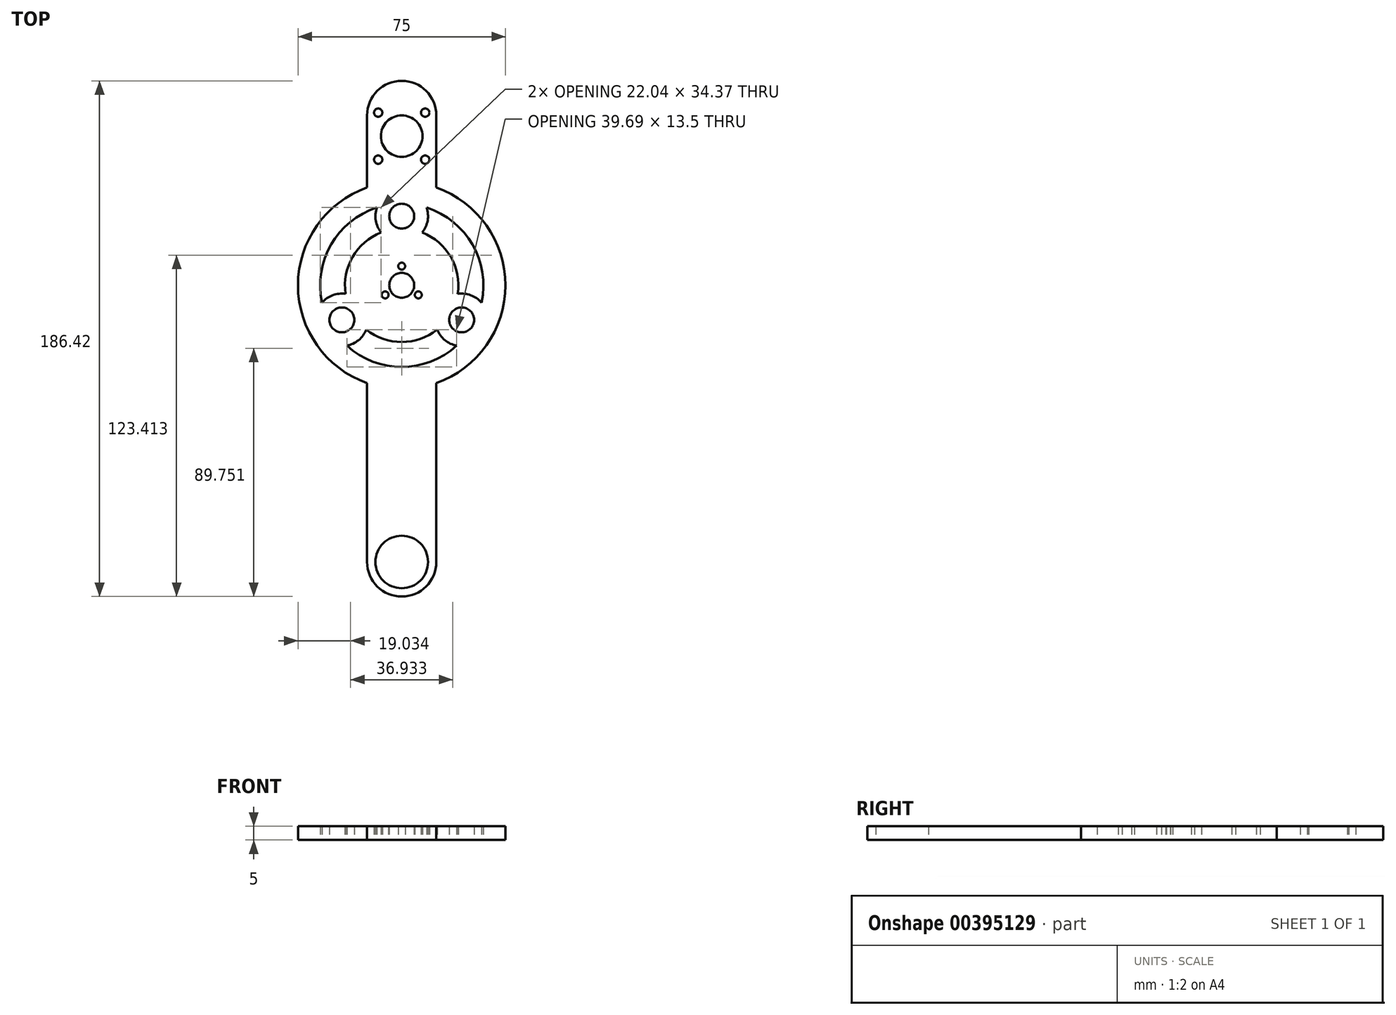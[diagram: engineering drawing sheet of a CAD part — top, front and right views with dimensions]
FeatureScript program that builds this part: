
annotation { "Feature Type Name" : "Feature", "Feature Type Description" : "" }
export const myFeature = defineFeature(function(context is Context, id is Id, definition is map)
    precondition{}
    {
        {
            var Q0;
            Q0=qCreatedBy(makeId("Top.planeOp"),FACE);
            var sketch = newSketch(context, id + "F0", { "sketchPlane" : qUnion([Q0])});
            skCircle(sketch, "E0", {"center": v(0, 0) * mm, "radius": 37.5 * mm});
            skLineSegment(sketch, "E1", {"start": v(-12.5, 35.36) * mm, "end": v(-12.5, 61.42) * mm});
            skArc(sketch, "E2", {"start": v(12.5, 61.42) * mm, "mid": v(0, 73.92) * mm, "end": v(-12.5, 61.42) * mm});
            skLineSegment(sketch, "E3", {"start": v(12.5, 61.42) * mm, "end": v(12.5, 35.36) * mm});
            skLineSegment(sketch, "E4", {"start": v(-12.5, -35.36) * mm, "end": v(-12.5, -100) * mm});
            skArc(sketch, "E5", {"start": v(-12.5, -100) * mm, "mid": v(0, -112.5) * mm, "end": v(12.5, -100) * mm});
            skLineSegment(sketch, "E6", {"start": v(12.5, -100) * mm, "end": v(12.5, -35.36) * mm});
            skCircle(sketch, "E7", {"center": v(-8.5, 45.42) * mm, "radius": 1.5 * mm});
            skCircle(sketch, "E8", {"center": v(8.5, 45.42) * mm, "radius": 1.5 * mm});
            skCircle(sketch, "E9", {"center": v(0, 53.92) * mm, "radius": 7.5 * mm});
            skCircle(sketch, "E10", {"center": v(8.5, 62.42) * mm, "radius": 1.5 * mm});
            skLineSegment(sketch, "E11", {"start": v(8.5, 45.42) * mm, "end": v(0, 53.92) * mm, "construction": true});
            skCircle(sketch, "E12", {"center": v(-8.5, 62.42) * mm, "radius": 1.5 * mm});
            skLineSegment(sketch, "E13", {"start": v(-8.5, 45.42) * mm, "end": v(0, 53.92) * mm, "construction": true});
            skLineSegment(sketch, "E14", {"start": v(-8.5, 62.42) * mm, "end": v(0, 53.92) * mm, "construction": true});
            skLineSegment(sketch, "E15", {"start": v(-12.5, 35.36) * mm, "end": v(12.5, 35.36) * mm, "construction": true});
            skLineSegment(sketch, "E16", {"start": v(12.5, -35.36) * mm, "end": v(-12.5, -35.36) * mm, "construction": true});
            skLineSegment(sketch, "E17", {"start": v(0, 0) * mm, "end": v(0, -18.97) * mm, "construction": true});
            skCircle(sketch, "E18", {"center": v(0, 0) * mm, "radius": 4.5 * mm});
            skLineSegment(sketch, "E19", {"start": v(8.5, 62.42) * mm, "end": v(0, 53.92) * mm, "construction": true});
            skCircle(sketch, "E20", {"center": v(0, -100) * mm, "radius": 9.5 * mm});
            skCircle(sketch, "E21", {"center": v(0, 6.93) * mm, "radius": 1.25 * mm});
            skCircle(sketch, "E22", {"center": v(6, -3.46) * mm, "radius": 1.25 * mm});
            skCircle(sketch, "E23", {"center": v(-6, -3.46) * mm, "radius": 1.25 * mm});
            skCircle(sketch, "E24", {"center": v(0, 0) * mm, "radius": 10 * mm});
            skLineSegment(sketch, "E25", {"start": v(-6, -3.46) * mm, "end": v(0, 6.93) * mm, "construction": true});
            skLineSegment(sketch, "E26", {"start": v(6, -3.46) * mm, "end": v(0, 6.93) * mm, "construction": true});
            skLineSegment(sketch, "E27", {"start": v(-6, -3.46) * mm, "end": v(6, -3.46) * mm, "construction": true});
            skLineSegment(sketch, "E28", {"start": v(-6, -3.46) * mm, "end": v(0, 0) * mm, "construction": true});
            skLineSegment(sketch, "E29", {"start": v(0, 6.93) * mm, "end": v(0, 0) * mm, "construction": true});
            skLineSegment(sketch, "E30", {"start": v(0, 0) * mm, "end": v(6, -3.46) * mm, "construction": true});
            skCircle(sketch, "E31", {"center": v(0, 25) * mm, "radius": 4.5 * mm});
            skCircle(sketch, "E32", {"center": v(21.65, -12.5) * mm, "radius": 4.5 * mm});
            skCircle(sketch, "E33", {"center": v(-21.65, -12.5) * mm, "radius": 4.5 * mm});
            skLineSegment(sketch, "E34", {"start": v(0, 25) * mm, "end": v(0, 6.93) * mm, "construction": true});
            skLineSegment(sketch, "E35", {"start": v(-21.65, -12.5) * mm, "end": v(-6, -3.46) * mm, "construction": true});
            skLineSegment(sketch, "E36", {"start": v(21.65, -12.5) * mm, "end": v(6, -3.46) * mm, "construction": true});
            skCircle(sketch, "E37", {"center": v(0, 25) * mm, "radius": 9.5 * mm});
            skCircle(sketch, "E38", {"center": v(-21.65, -12.5) * mm, "radius": 9.5 * mm});
            skCircle(sketch, "E39", {"center": v(21.65, -12.5) * mm, "radius": 9.5 * mm});
            skCircle(sketch, "E40", {"center": v(0, 0) * mm, "radius": 20.5 * mm});
            skCircle(sketch, "E41", {"center": v(0, 0) * mm, "radius": 29.5 * mm});
            skSolve(sketch);
        }
        {
            var Q0;
            Q0=qSketchRegion(id+"F0",true);
            var Q1;
            {var subQ0=sQuery(id+"F0.wireOp",EDGE,"55e76af4-ff7d-4902-8194-23b5d1213256");var subQ2=sQuery(id+"F0.wireOp",EDGE,"25387a36-7e12-4ac9-bd1b-64446be451f5");var subQ4=makeQuery(id+"F0.imprint","INTERSECT",VERTEX,{"disambiguationData":[OD(0.0)],"derivedFrom":[subQ2,subQ0]});Q1=makeQuery(id+"F0.imprint","IMPRINT",FACE,{"disambiguationData":[TD([[makeQuery(id+"F0.imprint","IMPRINT",EDGE,{"disambiguationData":[TD([[subQ4,-1.0]])],"derivedFrom":subQ2}),1.0]])]});}
            var Q2;
            Q2=makeQuery(id+"F0.imprint","IMPRINT",FACE,{"disambiguationData":[TD([[makeQuery(id+"F0.imprint","IMPRINT",EDGE,{"derivedFrom":sQuery(id+"F0.wireOp",EDGE,"E18")}),-1.0]])]});
            var Q3;
            {var subQ0=sQuery(id+"F0.wireOp",EDGE,"55e76af4-ff7d-4902-8194-23b5d1213256");var subQ3=sQuery(id+"F0.wireOp",EDGE,"25387a36-7e12-4ac9-bd1b-64446be451f5");var subQ4=makeQuery(id+"F0.imprint","INTERSECT",VERTEX,{"disambiguationData":[OD(0.0)],"derivedFrom":[subQ3,subQ0]});Q3=makeQuery(id+"F0.imprint","IMPRINT",FACE,{"disambiguationData":[TD([[makeQuery(id+"F0.imprint","IMPRINT",EDGE,{"disambiguationData":[TD([[subQ4,1.0]])],"derivedFrom":subQ3}),1.0]])]});}
            var Q4;
            {var subQ0=sQuery(id+"F0.wireOp",EDGE,"dd525a7c-7dce-4a06-8177-d9d2553b9335");var subQ2=sQuery(id+"F0.wireOp",EDGE,"25387a36-7e12-4ac9-bd1b-64446be451f5");var subQ4=makeQuery(id+"F0.imprint","INTERSECT",VERTEX,{"disambiguationData":[OD(0.0)],"derivedFrom":[subQ2,subQ0]});Q4=makeQuery(id+"F0.imprint","IMPRINT",FACE,{"disambiguationData":[TD([[makeQuery(id+"F0.imprint","IMPRINT",EDGE,{"disambiguationData":[TD([[subQ4,1.0]])],"derivedFrom":subQ2}),1.0]])]});}
            var Q5;
            {var subQ0=sQuery(id+"F0.wireOp",EDGE,"55e76af4-ff7d-4902-8194-23b5d1213256");var subQ3=sQuery(id+"F0.wireOp",EDGE,"25387a36-7e12-4ac9-bd1b-64446be451f5");var subQ4=makeQuery(id+"F0.imprint","INTERSECT",VERTEX,{"disambiguationData":[OD(1.0)],"derivedFrom":[subQ3,subQ0]});Q5=makeQuery(id+"F0.imprint","IMPRINT",FACE,{"disambiguationData":[TD([[makeQuery(id+"F0.imprint","IMPRINT",EDGE,{"disambiguationData":[TD([[subQ4,-1.0]])],"derivedFrom":subQ3}),1.0]])]});}
            var Q6;
            {var subQ3=sQuery(id+"F0.wireOp",EDGE,"b7f10987-ea30-4f7d-9cbb-5c5b287627f4");var subQ5=sQuery(id+"F0.wireOp",EDGE,"dd525a7c-7dce-4a06-8177-d9d2553b9335");var subQ7=makeQuery(id+"F0.imprint","INTERSECT",VERTEX,{"disambiguationData":[OD(0.0)],"derivedFrom":[subQ3,subQ5]});Q6=makeQuery(id+"F0.imprint","IMPRINT",FACE,{"disambiguationData":[TD([[makeQuery(id+"F0.imprint","IMPRINT",EDGE,{"disambiguationData":[TD([[subQ7,1.0]])],"derivedFrom":subQ3}),1.0]])]});}
            var Q7;
            {var subQ0=sQuery(id+"F0.wireOp",EDGE,"55e76af4-ff7d-4902-8194-23b5d1213256");var subQ2=sQuery(id+"F0.wireOp",EDGE,"b7f10987-ea30-4f7d-9cbb-5c5b287627f4");var subQ3=makeQuery(id+"F0.imprint","INTERSECT",VERTEX,{"disambiguationData":[OD(0.0)],"derivedFrom":[subQ2,subQ0]});Q7=makeQuery(id+"F0.imprint","IMPRINT",FACE,{"disambiguationData":[TD([[makeQuery(id+"F0.imprint","IMPRINT",EDGE,{"disambiguationData":[TD([[subQ3,1.0]])],"derivedFrom":subQ2}),1.0]])]});}
            var Q8;
            {var subQ3=sQuery(id+"F0.wireOp",EDGE,"b7f10987-ea30-4f7d-9cbb-5c5b287627f4");var subQ5=sQuery(id+"F0.wireOp",EDGE,"dd525a7c-7dce-4a06-8177-d9d2553b9335");var subQ7=makeQuery(id+"F0.imprint","INTERSECT",VERTEX,{"disambiguationData":[OD(1.0)],"derivedFrom":[subQ3,subQ5]});Q8=makeQuery(id+"F0.imprint","IMPRINT",FACE,{"disambiguationData":[TD([[makeQuery(id+"F0.imprint","IMPRINT",EDGE,{"disambiguationData":[TD([[subQ7,-1.0]])],"derivedFrom":subQ3}),1.0]])]});}
            var Q9;
            {var subQ0=sQuery(id+"F0.wireOp",EDGE,"dd525a7c-7dce-4a06-8177-d9d2553b9335");var subQ2=sQuery(id+"F0.wireOp",EDGE,"b7f10987-ea30-4f7d-9cbb-5c5b287627f4");var subQ3=makeQuery(id+"F0.imprint","INTERSECT",VERTEX,{"disambiguationData":[OD(0.0)],"derivedFrom":[subQ2,subQ0]});Q9=makeQuery(id+"F0.imprint","IMPRINT",FACE,{"disambiguationData":[TD([[makeQuery(id+"F0.imprint","IMPRINT",EDGE,{"disambiguationData":[TD([[subQ3,-1.0]])],"derivedFrom":subQ2}),1.0]])]});}
            var Q10;
            {var subQ3=sQuery(id+"F0.wireOp",EDGE,"a940a7dc-2615-4278-8fdb-ebe8dec3286c");var subQ5=sQuery(id+"F0.wireOp",EDGE,"dd525a7c-7dce-4a06-8177-d9d2553b9335");var subQ7=makeQuery(id+"F0.imprint","INTERSECT",VERTEX,{"disambiguationData":[OD(1.0)],"derivedFrom":[subQ3,subQ5]});Q10=makeQuery(id+"F0.imprint","IMPRINT",FACE,{"disambiguationData":[TD([[makeQuery(id+"F0.imprint","IMPRINT",EDGE,{"disambiguationData":[TD([[subQ7,1.0]])],"derivedFrom":subQ3}),1.0]])]});}
            var Q11;
            {var subQ0=sQuery(id+"F0.wireOp",EDGE,"dd525a7c-7dce-4a06-8177-d9d2553b9335");var subQ2=sQuery(id+"F0.wireOp",EDGE,"a940a7dc-2615-4278-8fdb-ebe8dec3286c");var subQ4=makeQuery(id+"F0.imprint","INTERSECT",VERTEX,{"disambiguationData":[OD(0.0)],"derivedFrom":[subQ2,subQ0]});Q11=makeQuery(id+"F0.imprint","IMPRINT",FACE,{"disambiguationData":[TD([[makeQuery(id+"F0.imprint","IMPRINT",EDGE,{"disambiguationData":[TD([[subQ4,1.0]])],"derivedFrom":subQ2}),1.0]])]});}
            var Q12;
            {var subQ3=sQuery(id+"F0.wireOp",EDGE,"a940a7dc-2615-4278-8fdb-ebe8dec3286c");var subQ5=sQuery(id+"F0.wireOp",EDGE,"dd525a7c-7dce-4a06-8177-d9d2553b9335");var subQ7=makeQuery(id+"F0.imprint","INTERSECT",VERTEX,{"disambiguationData":[OD(0.0)],"derivedFrom":[subQ3,subQ5]});Q12=makeQuery(id+"F0.imprint","IMPRINT",FACE,{"disambiguationData":[TD([[makeQuery(id+"F0.imprint","IMPRINT",EDGE,{"disambiguationData":[TD([[subQ7,-1.0]])],"derivedFrom":subQ3}),1.0]])]});}
            var Q13;
            {var subQ0=sQuery(id+"F0.wireOp",EDGE,"55e76af4-ff7d-4902-8194-23b5d1213256");var subQ2=sQuery(id+"F0.wireOp",EDGE,"a940a7dc-2615-4278-8fdb-ebe8dec3286c");var subQ4=makeQuery(id+"F0.imprint","INTERSECT",VERTEX,{"disambiguationData":[OD(0.0)],"derivedFrom":[subQ2,subQ0]});Q13=makeQuery(id+"F0.imprint","IMPRINT",FACE,{"disambiguationData":[TD([[makeQuery(id+"F0.imprint","IMPRINT",EDGE,{"disambiguationData":[TD([[subQ4,-1.0]])],"derivedFrom":subQ2}),1.0]])]});}
            var Q14;
            {var subQ0=sQuery(id+"F0.wireOp",EDGE,"E41");var subQ1=sQuery(id+"F0.wireOp",EDGE,"E38");var subQ4=makeQuery(id+"F0.imprint","INTERSECT",VERTEX,{"disambiguationData":[OD(0.0)],"derivedFrom":[subQ1,subQ0]});Q14=makeQuery(id+"F0.imprint","IMPRINT",FACE,{"disambiguationData":[TD([[makeQuery(id+"F0.imprint","IMPRINT",EDGE,{"disambiguationData":[TD([[subQ4,-1.0]])],"derivedFrom":subQ1}),1.0]])]});}
            var Q15;
            {var subQ0=sQuery(id+"F0.wireOp",EDGE,"E40");var subQ1=sQuery(id+"F0.wireOp",EDGE,"E38");var subQ4=makeQuery(id+"F0.imprint","INTERSECT",VERTEX,{"disambiguationData":[OD(0.0)],"derivedFrom":[subQ1,subQ0]});Q15=makeQuery(id+"F0.imprint","IMPRINT",FACE,{"disambiguationData":[TD([[makeQuery(id+"F0.imprint","IMPRINT",EDGE,{"disambiguationData":[TD([[subQ4,1.0]])],"derivedFrom":subQ1}),1.0]])]});}
            var Q16;
            {var subQ3=sQuery(id+"F0.wireOp",EDGE,"E33");var subQ5=sQuery(id+"F0.wireOp",EDGE,"E40");var subQ7=makeQuery(id+"F0.imprint","INTERSECT",VERTEX,{"derivedFrom":[subQ3,subQ5]});Q16=makeQuery(id+"F0.imprint","IMPRINT",FACE,{"disambiguationData":[TD([[makeQuery(id+"F0.imprint","IMPRINT",EDGE,{"disambiguationData":[TD([[subQ7,1.0]])],"derivedFrom":subQ3}),-1.0]])]});}
            var Q17;
            {var subQ3=sQuery(id+"F0.wireOp",EDGE,"E33");var subQ5=sQuery(id+"F0.wireOp",EDGE,"E40");var subQ7=makeQuery(id+"F0.imprint","INTERSECT",VERTEX,{"derivedFrom":[subQ3,subQ5]});Q17=makeQuery(id+"F0.imprint","IMPRINT",FACE,{"disambiguationData":[TD([[makeQuery(id+"F0.imprint","IMPRINT",EDGE,{"disambiguationData":[TD([[subQ7,-1.0]])],"derivedFrom":subQ3}),-1.0]])]});}
            var Q18;
            {var subQ3=sQuery(id+"F0.wireOp",EDGE,"E32");var subQ5=sQuery(id+"F0.wireOp",EDGE,"E40");var subQ7=makeQuery(id+"F0.imprint","INTERSECT",VERTEX,{"derivedFrom":[subQ3,subQ5]});Q18=makeQuery(id+"F0.imprint","IMPRINT",FACE,{"disambiguationData":[TD([[makeQuery(id+"F0.imprint","IMPRINT",EDGE,{"disambiguationData":[TD([[subQ7,-1.0]])],"derivedFrom":subQ3}),-1.0]])]});}
            var Q19;
            {var subQ3=sQuery(id+"F0.wireOp",EDGE,"E32");var subQ5=sQuery(id+"F0.wireOp",EDGE,"E40");var subQ7=makeQuery(id+"F0.imprint","INTERSECT",VERTEX,{"derivedFrom":[subQ3,subQ5]});Q19=makeQuery(id+"F0.imprint","IMPRINT",FACE,{"disambiguationData":[TD([[makeQuery(id+"F0.imprint","IMPRINT",EDGE,{"disambiguationData":[TD([[subQ7,1.0]])],"derivedFrom":subQ3}),-1.0]])]});}
            var Q20;
            {var subQ0=sQuery(id+"F0.wireOp",EDGE,"E40");var subQ1=sQuery(id+"F0.wireOp",EDGE,"E39");var subQ2=makeQuery(id+"F0.imprint","INTERSECT",VERTEX,{"disambiguationData":[OD(0.0)],"derivedFrom":[subQ1,subQ0]});Q20=makeQuery(id+"F0.imprint","IMPRINT",FACE,{"disambiguationData":[TD([[makeQuery(id+"F0.imprint","IMPRINT",EDGE,{"disambiguationData":[TD([[subQ2,-1.0]])],"derivedFrom":subQ1}),1.0]])]});}
            var Q21;
            {var subQ0=sQuery(id+"F0.wireOp",EDGE,"E41");var subQ1=sQuery(id+"F0.wireOp",EDGE,"E39");var subQ2=makeQuery(id+"F0.imprint","INTERSECT",VERTEX,{"disambiguationData":[OD(0.0)],"derivedFrom":[subQ1,subQ0]});Q21=makeQuery(id+"F0.imprint","IMPRINT",FACE,{"disambiguationData":[TD([[makeQuery(id+"F0.imprint","IMPRINT",EDGE,{"disambiguationData":[TD([[subQ2,1.0]])],"derivedFrom":subQ1}),1.0]])]});}
            var Q22;
            {var subQ0=sQuery(id+"F0.wireOp",EDGE,"E40");var subQ1=sQuery(id+"F0.wireOp",EDGE,"E37");var subQ2=makeQuery(id+"F0.imprint","INTERSECT",VERTEX,{"disambiguationData":[OD(0.0)],"derivedFrom":[subQ1,subQ0]});Q22=makeQuery(id+"F0.imprint","IMPRINT",FACE,{"disambiguationData":[TD([[makeQuery(id+"F0.imprint","IMPRINT",EDGE,{"disambiguationData":[TD([[subQ2,-1.0]])],"derivedFrom":subQ1}),1.0]])]});}
            var Q23;
            {var subQ3=sQuery(id+"F0.wireOp",EDGE,"E31");var subQ5=sQuery(id+"F0.wireOp",EDGE,"E40");var subQ7=makeQuery(id+"F0.imprint","INTERSECT",VERTEX,{"derivedFrom":[subQ3,subQ5]});Q23=makeQuery(id+"F0.imprint","IMPRINT",FACE,{"disambiguationData":[TD([[makeQuery(id+"F0.imprint","IMPRINT",EDGE,{"disambiguationData":[TD([[subQ7,-1.0]])],"derivedFrom":subQ3}),-1.0]])]});}
            var Q24;
            {var subQ0=sQuery(id+"F0.wireOp",EDGE,"E41");var subQ1=sQuery(id+"F0.wireOp",EDGE,"E37");var subQ2=makeQuery(id+"F0.imprint","INTERSECT",VERTEX,{"disambiguationData":[OD(0.0)],"derivedFrom":[subQ1,subQ0]});Q24=makeQuery(id+"F0.imprint","IMPRINT",FACE,{"disambiguationData":[TD([[makeQuery(id+"F0.imprint","IMPRINT",EDGE,{"disambiguationData":[TD([[subQ2,1.0]])],"derivedFrom":subQ1}),1.0]])]});}
            var Q25;
            {var subQ3=sQuery(id+"F0.wireOp",EDGE,"E31");var subQ5=sQuery(id+"F0.wireOp",EDGE,"E40");var subQ7=makeQuery(id+"F0.imprint","INTERSECT",VERTEX,{"derivedFrom":[subQ3,subQ5]});Q25=makeQuery(id+"F0.imprint","IMPRINT",FACE,{"disambiguationData":[TD([[makeQuery(id+"F0.imprint","IMPRINT",EDGE,{"disambiguationData":[TD([[subQ7,1.0]])],"derivedFrom":subQ3}),-1.0]])]});}
            var Q26;
            Q26=makeQuery(id+"F0.imprint","IMPRINT",FACE,{"disambiguationData":[TD([[makeQuery(id+"F0.imprint","IMPRINT",EDGE,{"derivedFrom":sQuery(id+"F0.wireOp",EDGE,"E24")}),-1.0]])]});
            extrude(context, id + "F1", {"entities" : qUnion([Q0, Q1, Q2, Q3, Q4, Q5, Q6, Q7, Q8, Q9, Q10, Q11, Q12, Q13, Q14, Q15, Q16, Q17, Q18, Q19, Q20, Q21, Q22, Q23, Q24, Q25, Q26]), "depth" : 5 * mm});
        }
    });
